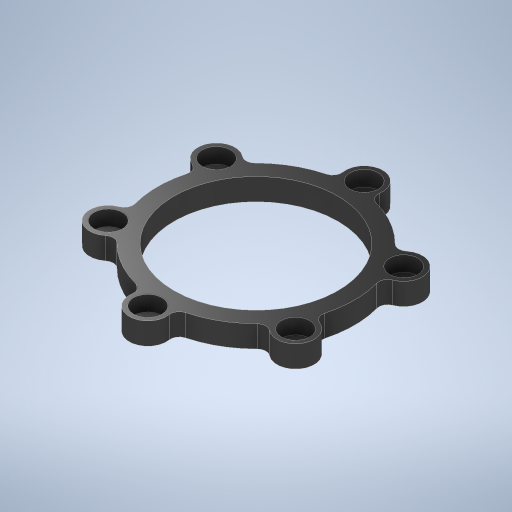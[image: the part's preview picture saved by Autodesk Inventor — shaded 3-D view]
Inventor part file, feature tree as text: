
AUTODESK INVENTOR PART (.ipt)
format: ipt  version: 2024.2 (Build 282272000, 272)  size: 411,136 bytes
history: native  units: mm
features: other x4, sketch x2, hole x2, extrude x1, fillet x1
ambient origin geometry x8: Origin, YZ Plane, XZ Plane, XY Plane, X Axis, Y Axis, Z Axis, Center Point
bodies: Solid1 (feature_tree)
feature tree (10):
  other  "CrossRollerBearingOuterSupportStand.ipt"
  sketch  "Sketch2"  dims[d4=3.5mm d5=6.0mm d6=6.5mm d7=3.5mm d8=90.0deg d9=8.0mm d10=20.594885mm d11=2.0mm d12=37.5mm d13=6.0mm d14=6.5mm d15=3.5mm d16=90.0deg d17=8.0mm d18=20.594885mm]
  extrude  "Extrusion1"  Depth=5.0mm TaperAngle=0.0deg
  hole  "Hole1"  [1 undecoded]
  hole  "Hole2"  [1 undecoded]
  fillet  "Fillet1"  [1 undecoded]
  sketch  "Sketch1"  dims[d0=10.0mm d2=5.0mm d3=0.0mm]
  other  "TaggingFeature1"
  other  "Solid1::CrossRollerBearingOuterSupportStand.ipt"
  other  "Srf2"
note: 3 required parameter values undecoded (feature->parameter linkage not recoverable at this tier; creation-order binding heuristic only, values carry confidence <= 0.55)
